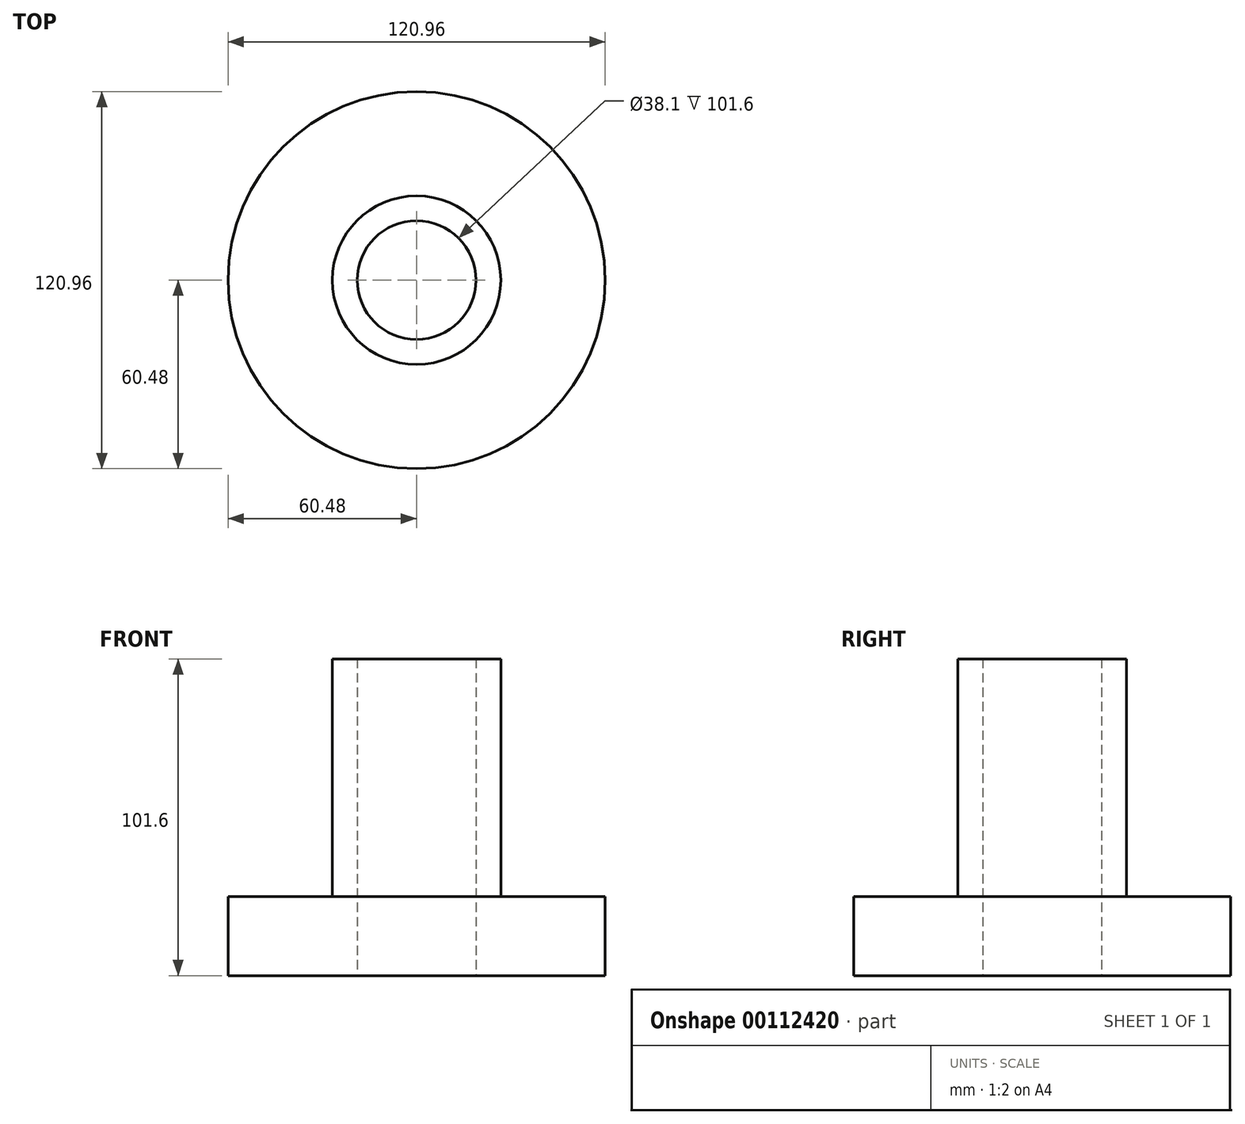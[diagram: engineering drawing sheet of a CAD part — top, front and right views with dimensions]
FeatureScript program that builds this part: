
annotation { "Feature Type Name" : "Feature", "Feature Type Description" : "" }
export const myFeature = defineFeature(function(context is Context, id is Id, definition is map)
    precondition{}
    {
        {
            var Q0;
            Q0=qCreatedBy(makeId("Top.planeOp"),FACE);
            var sketch = newSketch(context, id + "F0", { "sketchPlane" : qUnion([Q0])});
            skCircle(sketch, "E0", {"center": v(0, 0) * mm, "radius": 60.48 * mm});
            skSolve(sketch);
        }
        {
            var Q0;
            Q0 = qSketchRegion(id + "F0", true);
            extrude(context, id + "F1", {"entities" : qUnion([Q0]), "depth" : 25.4 * mm});
        }
        {
            var Q0;
            Q0=makeQuery(id+"F1.opExtrude","CAP_FACE",FACE,{"disambiguationData":[OSD([sQuery(id+"F0.wireOp",EDGE,"E0")])],"isStart":false});
            var sketch = newSketch(context, id + "F2", { "sketchPlane" : qUnion([Q0])});
            skCircle(sketch, "E1", {"center": v(0, 0) * mm, "radius": 27.03 * mm});
            skSolve(sketch);
        }
        {
            var Q0;
            Q0 = qSketchRegion(id + "F2", true);
            extrude(context, id + "F3", {"entities" : qUnion([Q0]), "operationType" : NewBodyOperationType.ADD, "depth" : 76.2 * mm});
        }
        {
            var Q0;
            Q0=qCreatedBy(makeId("Top.planeOp"),FACE);
            var sketch = newSketch(context, id + "F4", { "sketchPlane" : qUnion([Q0])});
            skCircle(sketch, "E2", {"center": v(0, 0) * mm, "radius": 17.73 * mm});
            skSolve(sketch);
        }
        {
            var Q0;
            Q0=sQuery(id+"F4.wireOp",VERTEX,"E2.center");
            var Q1;
            Q1=makeQuery(id+"F1.opExtrude","SWEPT_BODY",BODY,{"disambiguationData":[OSD([sQuery(id+"F0.wireOp",EDGE,"E0")])]});
            hole(context, id + "F5", {"style" : HoleStyle.SIMPLE, "endStyle" : HoleEndStyle.THROUGH, "oppositeDirection" : true, "holeDiameter" : 38.1 * mm, "locations" : qUnion([Q0]), "scope" : qUnion([Q1]), "isTappedThrough" : true});
        }
    });
